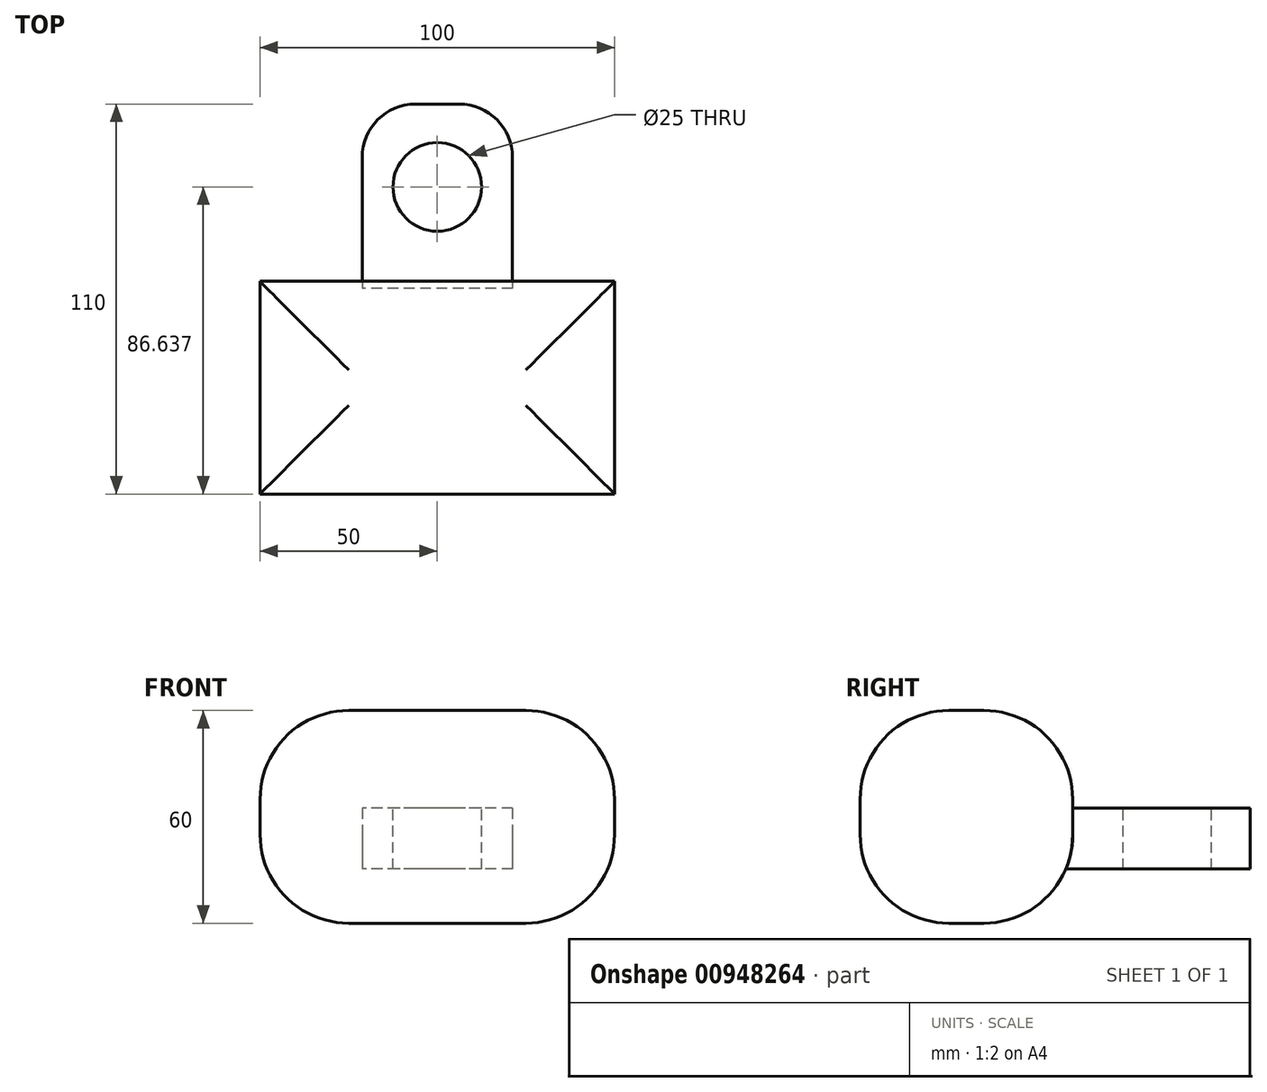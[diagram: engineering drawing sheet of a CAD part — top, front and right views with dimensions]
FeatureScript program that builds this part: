
annotation { "Feature Type Name" : "Feature", "Feature Type Description" : "" }
export const myFeature = defineFeature(function(context is Context, id is Id, definition is map)
    precondition{}
    {
        {
            var Q0;
            Q0=qCreatedBy(makeId("Top.planeOp"),FACE);
            var sketch = newSketch(context, id + "F0", { "sketchPlane" : qUnion([Q0])});
            skLineSegment(sketch, "E0.bottom", {"start": v(-50, -30) * mm, "end": v(50, -30) * mm});
            skLineSegment(sketch, "E0.top", {"start": v(-50, 30) * mm, "end": v(50, 30) * mm});
            skLineSegment(sketch, "E0.left", {"start": v(-50, -30) * mm, "end": v(-50, 30) * mm});
            skLineSegment(sketch, "E0.right", {"start": v(50, -30) * mm, "end": v(50, 30) * mm});
            skPoint(sketch, "E0.middle", {"position": v(0, 0) * mm});
            skSolve(sketch);
        }
        {
            var Q0;
            Q0=makeQuery(id+"F0.imprint","IMPRINT",FACE,{"disambiguationData":[TD([[makeQuery(id+"F0.imprint","IMPRINT",EDGE,{"derivedFrom":sQuery(id+"F0.wireOp",EDGE,"E0.bottom")}),1.0]])]});
            extrude(context, id + "F1", {"entities" : qUnion([Q0]), "depth" : 60 * mm, "offsetDistance" : 25 * mm});
        }
        {
            var Q0;
            Q0=makeQuery(id+"F1.opExtrude","SWEPT_FACE",FACE,{"disambiguationData":[OSD([sQuery(id+"F0.wireOp",EDGE,"E0.top")])]});
            var sketch = newSketch(context, id + "F2", { "sketchPlane" : qUnion([Q0])});
            skLineSegment(sketch, "E1.bottom", {"start": v(-21.19, 32.41) * mm, "end": v(21.19, 32.41) * mm});
            skLineSegment(sketch, "E1.top", {"start": v(-21.19, 15.26) * mm, "end": v(21.19, 15.26) * mm});
            skLineSegment(sketch, "E1.left", {"start": v(-21.19, 32.41) * mm, "end": v(-21.19, 15.26) * mm});
            skLineSegment(sketch, "E1.right", {"start": v(21.19, 32.41) * mm, "end": v(21.19, 15.26) * mm});
            skPoint(sketch, "E1.middle", {"position": v(0, 23.84) * mm});
            skSolve(sketch);
        }
        {
            var Q0;
            Q0=makeQuery(id+"F2.imprint","IMPRINT",FACE,{"disambiguationData":[TD([[makeQuery(id+"F2.imprint","IMPRINT",EDGE,{"derivedFrom":sQuery(id+"F2.wireOp",EDGE,"E1.bottom")}),-1.0]])]});
            extrude(context, id + "F3", {"entities" : qUnion([Q0]), "operationType" : NewBodyOperationType.ADD, "depth" : 50 * mm, "offsetDistance" : 25 * mm});
        }
        {
            var Q0;
            Q0=makeQuery(id+"F3.opExtrude","SWEPT_FACE",FACE,{"disambiguationData":[OSD([sQuery(id+"F2.wireOp",EDGE,"E1.bottom")])]});
            var sketch = newSketch(context, id + "F4", { "sketchPlane" : qUnion([Q0])});
            skCircle(sketch, "E2", {"center": v(0, 56.64) * mm, "radius": 12.5 * mm});
            skPoint(sketch, "E3", {"position": v(0, 80) * mm});
            skSolve(sketch);
        }
        {
            var Q0;
            Q0=makeQuery(id+"F4.imprint","IMPRINT",FACE,{"disambiguationData":[TD([[makeQuery(id+"F4.imprint","IMPRINT",EDGE,{"derivedFrom":sQuery(id+"F4.wireOp",EDGE,"E2")}),1.0]])]});
            extrude(context, id + "F5", {"entities" : qUnion([Q0]), "operationType" : NewBodyOperationType.REMOVE, "endBound" : BoundingType.THROUGH_ALL, "oppositeDirection" : true, "depth" : 25 * mm, "offsetDistance" : 25 * mm});
        }
        {
            var Q0;
            Q0=makeQuery(id+"F1.opExtrude","CAP_FACE",FACE,{"disambiguationData":[OSD([sQuery(id+"F0.wireOp",EDGE,"E0.bottom"),sQuery(id+"F0.wireOp",EDGE,"E0.top"),sQuery(id+"F0.wireOp",EDGE,"E0.left"),sQuery(id+"F0.wireOp",EDGE,"E0.right")])],"isStart":false});
            var Q1;
            Q1=makeQuery(id+"F1.opExtrude","CAP_FACE",FACE,{"disambiguationData":[OSD([sQuery(id+"F0.wireOp",EDGE,"E0.bottom"),sQuery(id+"F0.wireOp",EDGE,"E0.top"),sQuery(id+"F0.wireOp",EDGE,"E0.left"),sQuery(id+"F0.wireOp",EDGE,"E0.right")])],"isStart":true});
            fillet(context, id + "F6", {"entities" : qUnion([Q0, Q1]), "radius" : 25 * mm, "tangentPropagation" : true, "defaultsChanged" : false, "vertexSettings" : [], "allowEdgeOverflow" : false});
        }
        {
            var Q0;
            Q0=makeQuery(id+"F3.opExtrude","CAP_EDGE",EDGE,{"disambiguationData":[OSD([sQuery(id+"F2.wireOp",EDGE,"E1.right")])],"isStart":false});
            var Q1;
            Q1=makeQuery(id+"F3.opExtrude","CAP_EDGE",EDGE,{"disambiguationData":[OSD([sQuery(id+"F2.wireOp",EDGE,"E1.left")])],"isStart":false});
            fillet(context, id + "F7", {"entities" : qUnion([Q0, Q1]), "tangentPropagation" : true, "radius" : 15 * mm, "defaultsChanged" : true, "vertexSettings" : [], "allowEdgeOverflow" : false});
        }
    });
